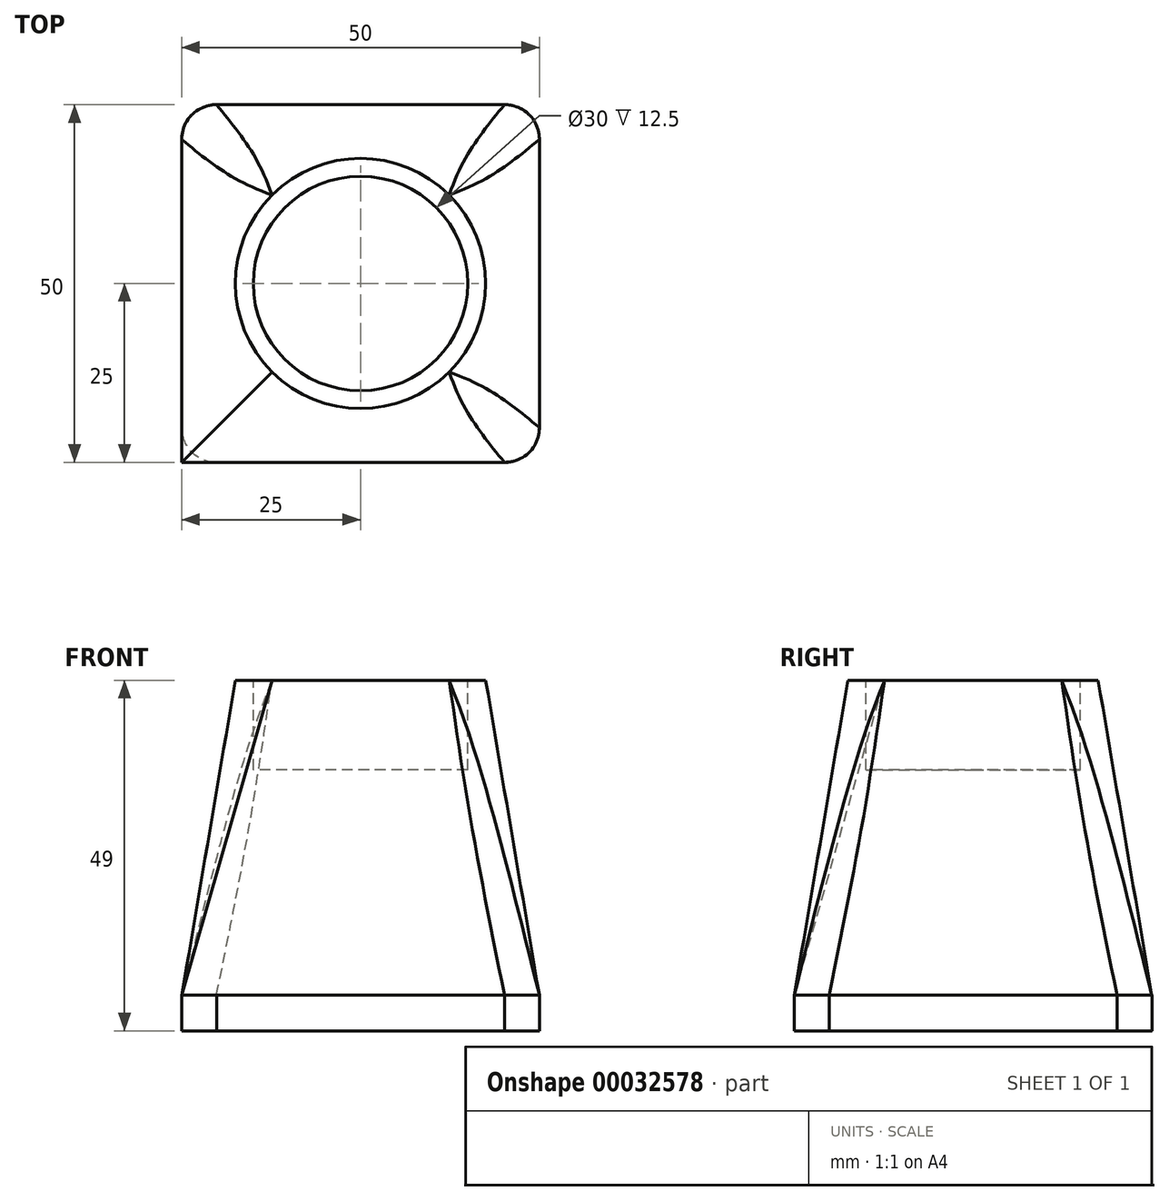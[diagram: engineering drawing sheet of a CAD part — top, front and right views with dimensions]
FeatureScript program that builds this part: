
annotation { "Feature Type Name" : "Feature", "Feature Type Description" : "" }
export const myFeature = defineFeature(function(context is Context, id is Id, definition is map)
    precondition{}
    {
        {
            var Q0;
            Q0=qCreatedBy(makeId("Top.planeOp"),FACE);
            var sketch = newSketch(context, id + "F0", { "sketchPlane" : qUnion([Q0])});
            skLineSegment(sketch, "E0.rect.bottom", {"start": v(-25, 25) * mm, "end": v(25, 25) * mm});
            skLineSegment(sketch, "E0.rect.top", {"start": v(-25, -25) * mm, "end": v(25, -25) * mm});
            skLineSegment(sketch, "E0.rect.left", {"start": v(-25, 25) * mm, "end": v(-25, -25) * mm});
            skLineSegment(sketch, "E0.rect.right", {"start": v(25, 25) * mm, "end": v(25, -25) * mm});
            skPoint(sketch, "E0.rect.middle", {"position": v(0, 0) * mm});
            skSolve(sketch);
        }
        {
            var Q0;
            Q0=qCreatedBy(makeId("Top.planeOp"),FACE);
            cPlane(context, id + "F1", {"entities" : qUnion([Q0]), "cplaneType" : CPlaneType.OFFSET, "offset" : 44 * mm, "width" : 150 * mm, "height" : 150 * mm});
        }
        {
            var Q0;
            Q0=qCreatedBy(id+"F1.planeOp",FACE);
            var sketch = newSketch(context, id + "F8", { "sketchPlane" : qUnion([Q0])});
            skCircle(sketch, "E1", {"center": v(0, 0) * mm, "radius": 17.5 * mm});
            skSolve(sketch);
        }
        {
            var Q0;
            Q0 = qSketchRegion(id + "F0", true);
            var Q1;
            Q1 = qSketchRegion(id + "F8", true);
            loft(context, id + "F2", {"sheetProfilesArray" : [{ "sheetProfileEntities" : qUnion([Q0]) }, { "sheetProfileEntities" : qUnion([Q1]) }]});
        }
        {
            var Q0;
            Q0=makeQuery(id+"F2.opLoft","CAP_FACE",FACE,{"disambiguationData":[OSD([makeQuery(id+"F8.imprint","IMPRINT",FACE,{"disambiguationData":[TD([[makeQuery(id+"F8.imprint","IMPRINT",EDGE,{"derivedFrom":sQuery(id+"F8.wireOp",EDGE,"E1")}),1.0]])]})])],"isStart":true});
            var sketch = newSketch(context, id + "F3", { "sketchPlane" : qUnion([Q0])});
            skCircle(sketch, "E2", {"center": v(0, 0) * mm, "radius": 15 * mm});
            skSolve(sketch);
        }
        {
            var Q0;
            Q0=makeQuery(id+"F3.imprint","IMPRINT",FACE,{"disambiguationData":[TD([[makeQuery(id+"F3.imprint","IMPRINT",EDGE,{"derivedFrom":sQuery(id+"F3.wireOp",EDGE,"E2")}),1.0]])]});
            extrude(context, id + "F4", {"entities" : qUnion([Q0]), "operationType" : NewBodyOperationType.REMOVE, "oppositeDirection" : true, "depth" : 12.5 * mm});
        }
        {
            var Q0;
            Q0=makeQuery(id+"F2.opLoft","SWEPT_EDGE",EDGE,{"disambiguationData":[OSD([sQuery(id+"F0.wireOp",EDGE,"E0.rect.top"),sQuery(id+"F0.wireOp",EDGE,"E0.rect.left"),sQuery(id+"F0.wireOp",EDGE,"E0.rect.right"),sQuery(id+"F8.wireOp",EDGE,"E1")])]});
            var Q1;
            Q1=makeQuery(id+"F2.opLoft","SWEPT_EDGE",EDGE,{"disambiguationData":[OSD([sQuery(id+"F0.wireOp",EDGE,"E0.rect.bottom"),sQuery(id+"F0.wireOp",EDGE,"E0.rect.left")])]});
            var Q2;
            Q2=makeQuery(id+"F2.opLoft","SWEPT_EDGE",EDGE,{"disambiguationData":[OSD([sQuery(id+"F0.wireOp",EDGE,"E0.rect.bottom"),sQuery(id+"F0.wireOp",EDGE,"E0.rect.top"),sQuery(id+"F0.wireOp",EDGE,"E0.rect.right"),sQuery(id+"F8.wireOp",EDGE,"E1")])]});
            var Q3;
            Q3=makeQuery(id+"F2.opLoft","SWEPT_EDGE",EDGE,{"disambiguationData":[OSD([sQuery(id+"F0.wireOp",EDGE,"E0.rect.bottom"),sQuery(id+"F0.wireOp",EDGE,"E0.rect.top"),sQuery(id+"F0.wireOp",EDGE,"E0.rect.left"),sQuery(id+"F8.wireOp",EDGE,"E1")])]});
            fillet(context, id + "F5", {"entities" : qUnion([Q0, Q1, Q2, Q3]), "radius" : 5 * mm, "tangentPropagation" : true, "allowEdgeOverflow" : false});
        }
        {
            var Q0;
            Q0=makeQuery(id+"F2.opLoft","CAP_FACE",FACE,{"disambiguationData":[OSD([makeQuery(id+"F0.imprint","IMPRINT",FACE,{"disambiguationData":[TD([[makeQuery(id+"F0.imprint","IMPRINT",EDGE,{"derivedFrom":sQuery(id+"F0.wireOp",EDGE,"E0.rect.bottom")}),-1.0]])]})])],"isStart":true});
            var sketch = newSketch(context, id + "F6", { "sketchPlane" : qUnion([Q0])});
            skFitSpline(sketch, "E3.0", {"points": [v(20.11, -25) * mm, v(6.7, -25) * mm, v(-6.7, -25) * mm, v(-20.11, -25) * mm]});
            skFitSpline(sketch, "E4.0", {"points": [v(20.11, -25) * mm, v(20.44, -25) * mm, v(20.91, -24.95) * mm, v(21.54, -24.8) * mm, v(22.15, -24.59) * mm, v(22.85, -24.22) * mm, v(23.48, -23.7) * mm, v(23.9, -23.23) * mm, v(24.2, -22.85) * mm, v(24.44, -22.43) * mm, v(24.64, -22) * mm, v(24.8, -21.55) * mm, v(24.95, -20.92) * mm, v(25, -20.44) * mm, v(25, -20.11) * mm]});
            skFitSpline(sketch, "E5.0", {"points": [v(25, 20.11) * mm, v(25, 6.7) * mm, v(25, -6.7) * mm, v(25, -20.11) * mm]});
            skFitSpline(sketch, "E6.0", {"points": [v(25, 20.11) * mm, v(25, 20.44) * mm, v(24.95, 20.91) * mm, v(24.8, 21.54) * mm, v(24.59, 22.15) * mm, v(24.22, 22.85) * mm, v(23.7, 23.48) * mm, v(23.23, 23.9) * mm, v(22.85, 24.2) * mm, v(22.43, 24.44) * mm, v(22, 24.64) * mm, v(21.55, 24.8) * mm, v(20.92, 24.95) * mm, v(20.44, 25) * mm, v(20.11, 25) * mm]});
            skFitSpline(sketch, "E7.0", {"points": [v(-20.11, 25) * mm, v(-6.7, 25) * mm, v(6.7, 25) * mm, v(20.11, 25) * mm]});
            skFitSpline(sketch, "E8.0", {"points": [v(-20.11, 25) * mm, v(-20.44, 25) * mm, v(-20.91, 24.95) * mm, v(-21.54, 24.8) * mm, v(-22.15, 24.59) * mm, v(-22.85, 24.22) * mm, v(-23.48, 23.7) * mm, v(-23.9, 23.23) * mm, v(-24.2, 22.85) * mm, v(-24.44, 22.43) * mm, v(-24.64, 22) * mm, v(-24.8, 21.55) * mm, v(-24.95, 20.92) * mm, v(-25, 20.44) * mm, v(-25, 20.11) * mm]});
            skFitSpline(sketch, "E9.0", {"points": [v(-25, -20.11) * mm, v(-25, -6.7) * mm, v(-25, 6.7) * mm, v(-25, 20.11) * mm]});
            skFitSpline(sketch, "E10.0", {"points": [v(-25, -20.11) * mm, v(-25, -20.44) * mm, v(-24.95, -20.91) * mm, v(-24.8, -21.54) * mm, v(-24.59, -22.15) * mm, v(-24.22, -22.85) * mm, v(-23.7, -23.48) * mm, v(-23.23, -23.9) * mm, v(-22.85, -24.2) * mm, v(-22.43, -24.44) * mm, v(-22, -24.64) * mm, v(-21.55, -24.8) * mm, v(-20.92, -24.95) * mm, v(-20.44, -25) * mm, v(-20.11, -25) * mm]});
            skSolve(sketch);
        }
        {
            var Q0;
            Q0 = qSketchRegion(id + "F6", true);
            extrude(context, id + "F7", {"entities" : qUnion([Q0]), "operationType" : NewBodyOperationType.ADD, "depth" : 5 * mm});
        }
    });
